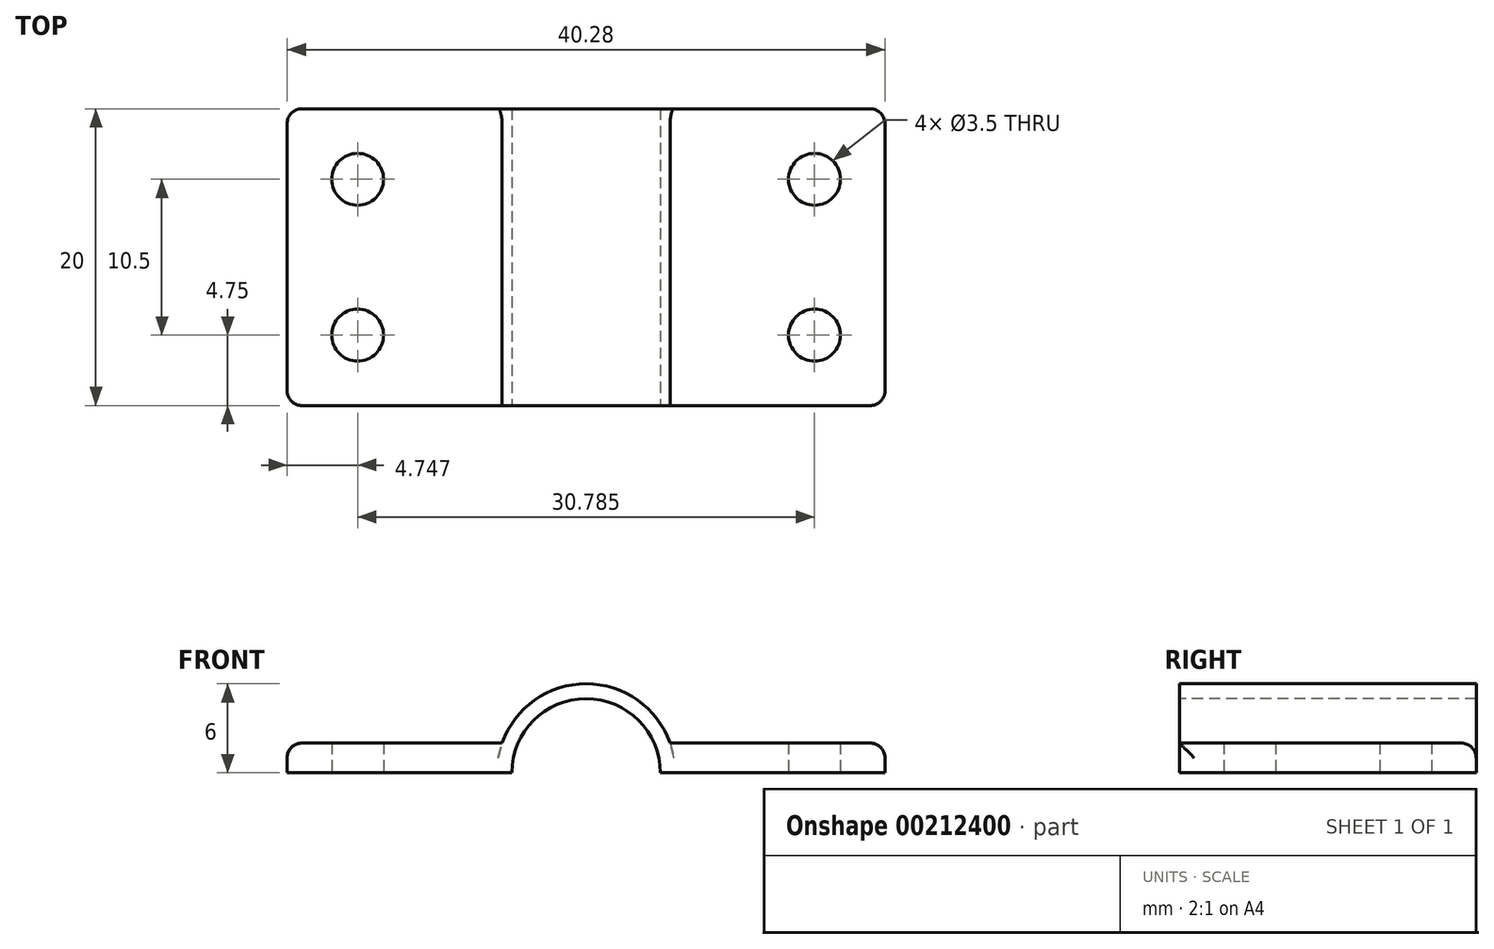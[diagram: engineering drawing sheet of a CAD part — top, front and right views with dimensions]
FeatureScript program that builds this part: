
annotation { "Feature Type Name" : "Feature", "Feature Type Description" : "" }
export const myFeature = defineFeature(function(context is Context, id is Id, definition is map)
    precondition{}
    {
        {
            var Q0;
            Q0=qCreatedBy(makeId("Top.planeOp"),FACE);
            var sketch = newSketch(context, id + "F0", { "sketchPlane" : qUnion([Q0])});
            skCircle(sketch, "E0", {"center": v(-15.4, 5.25) * mm, "radius": 1.75 * mm});
            skCircle(sketch, "E1", {"center": v(-15.4, -5.25) * mm, "radius": 1.75 * mm});
            skCircle(sketch, "E2.MirrorC", {"center": v(15.4, 5.25) * mm, "radius": 1.75 * mm});
            skCircle(sketch, "E3.MirrorC", {"center": v(15.4, -5.25) * mm, "radius": 1.75 * mm});
            skLineSegment(sketch, "E4.bottom", {"start": v(-20.14, 10) * mm, "end": v(20.14, 10) * mm});
            skLineSegment(sketch, "E4.top", {"start": v(-20.14, -10) * mm, "end": v(20.14, -10) * mm});
            skLineSegment(sketch, "E4.left", {"start": v(-20.14, 10) * mm, "end": v(-20.14, -10) * mm});
            skLineSegment(sketch, "E4.right", {"start": v(20.14, 10) * mm, "end": v(20.14, -10) * mm});
            skPoint(sketch, "E4.middle", {"position": v(0, 0) * mm});
            skSolve(sketch);
        }
        {
            var Q0;
            Q0=makeQuery(id+"F0.imprint","IMPRINT",FACE,{"disambiguationData":[TD([[makeQuery(id+"F0.imprint","IMPRINT",EDGE,{"derivedFrom":sQuery(id+"F0.wireOp",EDGE,"E0")}),-1.0]])]});
            extrude(context, id + "F1", {"entities" : qUnion([Q0]), "depth" : 10 * mm});
        }
        {
            var Q0;
            Q0=makeQuery(id+"F1.opExtrude","SWEPT_FACE",FACE,{"disambiguationData":[OSD([sQuery(id+"F0.wireOp",EDGE,"E4.top")])]});
            var sketch = newSketch(context, id + "F2", { "sketchPlane" : qUnion([Q0])});
            skCircle(sketch, "E5", {"center": v(0, 0) * mm, "radius": 5 * mm});
            skCircle(sketch, "E6", {"center": v(0, 0) * mm, "radius": 6 * mm});
            skLineSegment(sketch, "E7.bottom", {"start": v(-20.14, 0) * mm, "end": v(20.14, 0) * mm});
            skLineSegment(sketch, "E7.top", {"start": v(-20.14, 2) * mm, "end": v(20.14, 2) * mm});
            skLineSegment(sketch, "E7.left", {"start": v(-20.14, 0) * mm, "end": v(-20.14, 2) * mm});
            skLineSegment(sketch, "E7.right", {"start": v(20.14, 0) * mm, "end": v(20.14, 2) * mm});
            skSolve(sketch);
        }
        {
            var Q0;
            {var subQ0=sQuery(id+"F2.wireOp",EDGE,"E7.top");var subQ1=sQuery(id+"F2.wireOp",EDGE,"E5");var subQ2=makeQuery(id+"F2.imprint","INTERSECT",VERTEX,{"disambiguationData":[OD(0.0)],"derivedFrom":[subQ1,subQ0]});Q0=makeQuery(id+"F2.imprint","IMPRINT",FACE,{"disambiguationData":[TD([[makeQuery(id+"F2.imprint","IMPRINT",EDGE,{"disambiguationData":[TD([[subQ2,-1.0]])],"derivedFrom":subQ1}),1.0]])]});}
            var Q1;
            {var subQ0=sQuery(id+"F2.wireOp",EDGE,"E7.top");var subQ1=sQuery(id+"F2.wireOp",EDGE,"E5");var subQ2=makeQuery(id+"F2.imprint","INTERSECT",VERTEX,{"disambiguationData":[OD(0.0)],"derivedFrom":[subQ1,subQ0]});Q1=makeQuery(id+"F2.imprint","IMPRINT",FACE,{"disambiguationData":[TD([[makeQuery(id+"F2.imprint","IMPRINT",EDGE,{"disambiguationData":[TD([[subQ2,1.0]])],"derivedFrom":subQ1}),1.0]])]});}
            var Q2;
            {var subQ1=sQuery(id+"F0.wireOp",EDGE,"E4.top");var subQ6=makeQuery(id+"F1.opExtrude","CAP_EDGE",EDGE,{"disambiguationData":[OSD([subQ1])],"isStart":false});Q2=makeQuery(id+"F2.imprint","IMPRINT",FACE,{"disambiguationData":[TD([[makeQuery(id+"F2.imprint","IMPRINT",EDGE,{"derivedFrom":subQ6}),-1.0]])]});}
            extrude(context, id + "F3", {"entities" : qUnion([Q0, Q1, Q2]), "operationType" : NewBodyOperationType.REMOVE, "oppositeDirection" : true, "depth" : 25 * mm});
        }
        {
            var Q0;
            Q0=makeQuery(id+"F3.boolean.opBoolean","COPY",EDGE,{"derivedFrom":makeQuery(id+"F3.opExtrude","SWEPT_EDGE",EDGE,{"disambiguationData":[OSD([sQuery(id+"F0.wireOp",EDGE,"E4.top"),sQuery(id+"F0.wireOp",EDGE,"E4.left"),sQuery(id+"F2.wireOp",EDGE,"E7.top"),sQuery(id+"F2.wireOp",EDGE,"E7.left")])]})});
            var Q1;
            {var subQ0=sQuery(id+"F2.wireOp",EDGE,"E7.top");Q1=makeQuery(id+"F3.boolean.opBoolean","COPY",EDGE,{"derivedFrom":makeQuery(id+"F3.opExtrude","CAP_EDGE",EDGE,{"disambiguationData":[OSD([subQ0]),TDD([makeQuery(id+"F2.imprint","IMPRINT",EDGE,{"disambiguationData":[TD([[makeQuery(id+"F2.imprint","INTERSECT",VERTEX,{"disambiguationData":[OD(1.0)],"derivedFrom":[sQuery(id+"F2.wireOp",EDGE,"E6"),subQ0]}),1.0]])],"derivedFrom":subQ0})])],"isStart":true})});}
            var Q2;
            {var subQ0=sQuery(id+"F2.wireOp",EDGE,"E7.top");Q2=makeQuery(id+"F3.boolean.opBoolean","INTERSECT",EDGE,{"derivedFrom":[makeQuery(id+"F1.opExtrude","SWEPT_FACE",FACE,{"disambiguationData":[OSD([sQuery(id+"F0.wireOp",EDGE,"E4.bottom")])]}),makeQuery(id+"F3.opExtrude","SWEPT_FACE",FACE,{"disambiguationData":[OSD([subQ0]),TDD([makeQuery(id+"F2.imprint","IMPRINT",EDGE,{"disambiguationData":[TD([[makeQuery(id+"F2.imprint","INTERSECT",VERTEX,{"disambiguationData":[OD(1.0)],"derivedFrom":[sQuery(id+"F2.wireOp",EDGE,"E6"),subQ0]}),1.0]])],"derivedFrom":subQ0})])]})]});}
            var Q3;
            {var subQ0=sQuery(id+"F2.wireOp",EDGE,"E7.top");Q3=makeQuery(id+"F3.boolean.opBoolean","INTERSECT",EDGE,{"derivedFrom":[makeQuery(id+"F1.opExtrude","SWEPT_FACE",FACE,{"disambiguationData":[OSD([sQuery(id+"F0.wireOp",EDGE,"E4.bottom")])]}),makeQuery(id+"F3.opExtrude","SWEPT_FACE",FACE,{"disambiguationData":[OSD([subQ0]),TDD([makeQuery(id+"F2.imprint","IMPRINT",EDGE,{"disambiguationData":[TD([[makeQuery(id+"F2.imprint","INTERSECT",VERTEX,{"disambiguationData":[OD(0.0)],"derivedFrom":[sQuery(id+"F2.wireOp",EDGE,"E6"),subQ0]}),-1.0]])],"derivedFrom":subQ0})])]})]});}
            var Q4;
            Q4=makeQuery(id+"F3.boolean.opBoolean","COPY",EDGE,{"derivedFrom":makeQuery(id+"F3.opExtrude","SWEPT_EDGE",EDGE,{"disambiguationData":[OSD([sQuery(id+"F0.wireOp",EDGE,"E4.top"),sQuery(id+"F0.wireOp",EDGE,"E4.right"),sQuery(id+"F2.wireOp",EDGE,"E7.top"),sQuery(id+"F2.wireOp",EDGE,"E7.right")])]})});
            var Q5;
            {var subQ0=sQuery(id+"F2.wireOp",EDGE,"E7.top");Q5=makeQuery(id+"F3.boolean.opBoolean","COPY",EDGE,{"derivedFrom":makeQuery(id+"F3.opExtrude","CAP_EDGE",EDGE,{"disambiguationData":[OSD([subQ0]),TDD([makeQuery(id+"F2.imprint","IMPRINT",EDGE,{"disambiguationData":[TD([[makeQuery(id+"F2.imprint","INTERSECT",VERTEX,{"disambiguationData":[OD(0.0)],"derivedFrom":[sQuery(id+"F2.wireOp",EDGE,"E6"),subQ0]}),-1.0]])],"derivedFrom":subQ0})])],"isStart":true})});}
            fillet(context, id + "F4", {"entities" : qUnion([Q0, Q1, Q2, Q3, Q4, Q5]), "radius" : 1 * mm, "tangentPropagation" : true, "allowEdgeOverflow" : false});
        }
        {
            var Q0;
            Q0=makeQuery(id+"F1.opExtrude","SWEPT_EDGE",EDGE,{"disambiguationData":[OSD([sQuery(id+"F0.wireOp",EDGE,"E4.top"),sQuery(id+"F0.wireOp",EDGE,"E4.right")])]});
            var Q1;
            Q1=makeQuery(id+"F1.opExtrude","SWEPT_EDGE",EDGE,{"disambiguationData":[OSD([sQuery(id+"F0.wireOp",EDGE,"E4.bottom"),sQuery(id+"F0.wireOp",EDGE,"E4.right")])]});
            var Q2;
            Q2=makeQuery(id+"F1.opExtrude","SWEPT_EDGE",EDGE,{"disambiguationData":[OSD([sQuery(id+"F0.wireOp",EDGE,"E4.bottom"),sQuery(id+"F0.wireOp",EDGE,"E4.left")])]});
            var Q3;
            Q3=makeQuery(id+"F1.opExtrude","SWEPT_EDGE",EDGE,{"disambiguationData":[OSD([sQuery(id+"F0.wireOp",EDGE,"E4.top"),sQuery(id+"F0.wireOp",EDGE,"E4.left")])]});
            fillet(context, id + "F5", {"entities" : qUnion([Q0, Q1, Q2, Q3]), "radius" : 1 * mm, "tangentPropagation" : true, "allowEdgeOverflow" : false});
        }
    });
